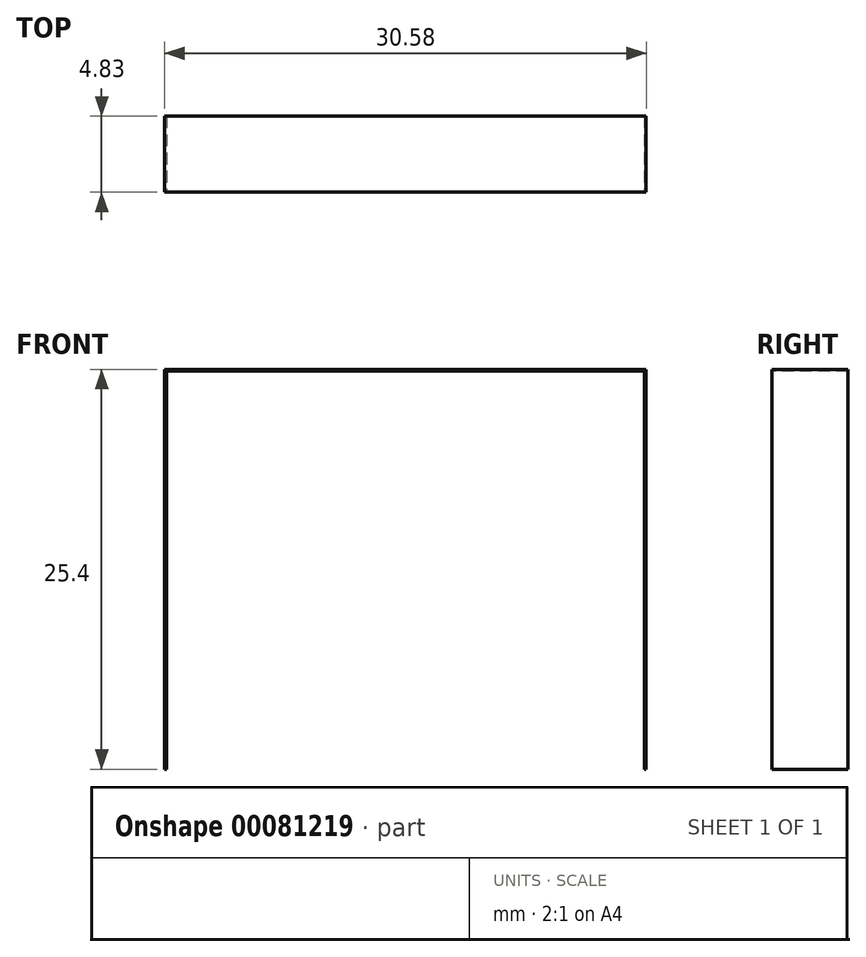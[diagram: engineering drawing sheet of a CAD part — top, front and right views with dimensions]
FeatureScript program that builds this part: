
annotation { "Feature Type Name" : "Feature", "Feature Type Description" : "" }
export const myFeature = defineFeature(function(context is Context, id is Id, definition is map)
    precondition{}
    {
        {
            var Q0;
            Q0=qCreatedBy(makeId("Top.planeOp"),FACE);
            var sketch = newSketch(context, id + "F0", { "sketchPlane" : qUnion([Q0])});
            skLineSegment(sketch, "E0.bottom", {"start": v(-15.19, -9.68) * mm, "end": v(15.19, -9.68) * mm});
            skLineSegment(sketch, "E0.top", {"start": v(-15.19, -4.85) * mm, "end": v(15.19, -4.85) * mm});
            skLineSegment(sketch, "E0.left", {"start": v(-15.19, -9.68) * mm, "end": v(-15.19, -4.85) * mm});
            skLineSegment(sketch, "E0.right", {"start": v(15.19, -9.68) * mm, "end": v(15.19, -4.85) * mm});
            skLineSegment(sketch, "E1.MirrorCS", {"start": v(-15.19, 4.85) * mm, "end": v(15.19, 4.85) * mm});
            skLineSegment(sketch, "E2.MirrorCS", {"start": v(-15.19, 9.68) * mm, "end": v(-15.19, 4.85) * mm});
            skLineSegment(sketch, "E3.MirrorCS", {"start": v(-15.19, 9.68) * mm, "end": v(15.19, 9.68) * mm});
            skLineSegment(sketch, "E4.MirrorCS", {"start": v(15.19, 9.68) * mm, "end": v(15.19, 4.85) * mm});
            skLineSegment(sketch, "E5.bottom", {"start": v(-15.19, 9.68) * mm, "end": v(-15.82, 9.68) * mm});
            skLineSegment(sketch, "E5.top", {"start": v(-15.19, 4.85) * mm, "end": v(-15.82, 4.85) * mm});
            skLineSegment(sketch, "E5.right", {"start": v(-15.82, 9.68) * mm, "end": v(-15.82, 4.85) * mm});
            skLineSegment(sketch, "E6.MirrorCS", {"start": v(-15.19, -4.85) * mm, "end": v(-15.82, -4.85) * mm});
            skLineSegment(sketch, "E7.MirrorCS", {"start": v(-15.82, -9.68) * mm, "end": v(-15.82, -4.85) * mm});
            skLineSegment(sketch, "E8.MirrorCS", {"start": v(-15.19, -9.68) * mm, "end": v(-15.82, -9.68) * mm});
            skLineSegment(sketch, "E9.MirrorCS", {"start": v(15.19, -4.85) * mm, "end": v(15.82, -4.85) * mm});
            skLineSegment(sketch, "E10.MirrorCS", {"start": v(15.82, -9.68) * mm, "end": v(15.82, -4.85) * mm});
            skLineSegment(sketch, "E11.MirrorCS", {"start": v(15.19, -9.68) * mm, "end": v(15.82, -9.68) * mm});
            skLineSegment(sketch, "E12.MirrorCS", {"start": v(15.19, 4.85) * mm, "end": v(15.82, 4.85) * mm});
            skLineSegment(sketch, "E13.MirrorCS", {"start": v(15.82, 9.68) * mm, "end": v(15.82, 4.85) * mm});
            skLineSegment(sketch, "E14.MirrorCS", {"start": v(15.19, 9.68) * mm, "end": v(15.82, 9.68) * mm});
            skSolve(sketch);
        }
        {
            var Q0;
            Q0=makeQuery(id+"F0.imprint","IMPRINT",FACE,{"disambiguationData":[TD([[makeQuery(id+"F0.imprint","IMPRINT",EDGE,{"derivedFrom":sQuery(id+"F0.wireOp",EDGE,"E1.MirrorCS")}),1.0]])]});
            extrude(context, id + "F1", {"entities" : qUnion([Q0]), "depth" : .10 * mm});
        }
        {
            var Q0;
            Q0=makeQuery(id+"F1.opExtrude","CAP_FACE",FACE,{"disambiguationData":[OSD([sQuery(id+"F0.wireOp",EDGE,"E1.MirrorCS"),sQuery(id+"F0.wireOp",EDGE,"E3.MirrorCS"),sQuery(id+"F0.wireOp",EDGE,"E2.MirrorCS"),sQuery(id+"F0.wireOp",EDGE,"E4.MirrorCS")])],"isStart":false});
            var sketch = newSketch(context, id + "F2", { "sketchPlane" : qUnion([Q0])});
            skLineSegment(sketch, "E15.bottom", {"start": v(15.19, 9.68) * mm, "end": v(15.29, 9.68) * mm});
            skLineSegment(sketch, "E15.top", {"start": v(15.19, 4.85) * mm, "end": v(15.29, 4.85) * mm});
            skLineSegment(sketch, "E15.left", {"start": v(15.19, 9.68) * mm, "end": v(15.19, 4.85) * mm});
            skLineSegment(sketch, "E15.right", {"start": v(15.29, 9.68) * mm, "end": v(15.29, 4.85) * mm});
            skLineSegment(sketch, "E16.MirrorCS", {"start": v(-15.19, 4.85) * mm, "end": v(-15.29, 4.85) * mm});
            skLineSegment(sketch, "E17.MirrorCS", {"start": v(-15.29, 9.68) * mm, "end": v(-15.29, 4.85) * mm});
            skLineSegment(sketch, "E18.MirrorCS", {"start": v(-15.19, 9.68) * mm, "end": v(-15.29, 9.68) * mm});
            skLineSegment(sketch, "E19.MirrorCS", {"start": v(-15.19, -9.68) * mm, "end": v(-15.29, -9.68) * mm});
            skLineSegment(sketch, "E20.MirrorCS", {"start": v(-15.29, -9.68) * mm, "end": v(-15.29, -4.85) * mm});
            skLineSegment(sketch, "E21.MirrorCS", {"start": v(-15.19, -4.85) * mm, "end": v(-15.29, -4.85) * mm});
            skLineSegment(sketch, "E22.MirrorCS", {"start": v(15.19, -4.85) * mm, "end": v(15.29, -4.85) * mm});
            skLineSegment(sketch, "E23.MirrorCS", {"start": v(15.29, -9.68) * mm, "end": v(15.29, -4.85) * mm});
            skLineSegment(sketch, "E24.MirrorCS", {"start": v(15.19, -9.68) * mm, "end": v(15.29, -9.68) * mm});
            skSolve(sketch);
        }
        {
            var Q0;
            Q0=makeQuery(id+"F2.imprint","IMPRINT",FACE,{"disambiguationData":[TD([[makeQuery(id+"F2.imprint","IMPRINT",EDGE,{"derivedFrom":sQuery(id+"F2.wireOp",EDGE,"E15.bottom")}),-1.0]])]});
            var Q1;
            Q1=makeQuery(id+"F2.imprint","IMPRINT",FACE,{"disambiguationData":[TD([[makeQuery(id+"F2.imprint","IMPRINT",EDGE,{"derivedFrom":sQuery(id+"F2.wireOp",EDGE,"E16.MirrorCS")}),-1.0]])]});
            extrude(context, id + "F3", {"entities" : qUnion([Q0, Q1]), "operationType" : NewBodyOperationType.ADD, "oppositeDirection" : true, "depth" : 25.4 * mm});
        }
    });
